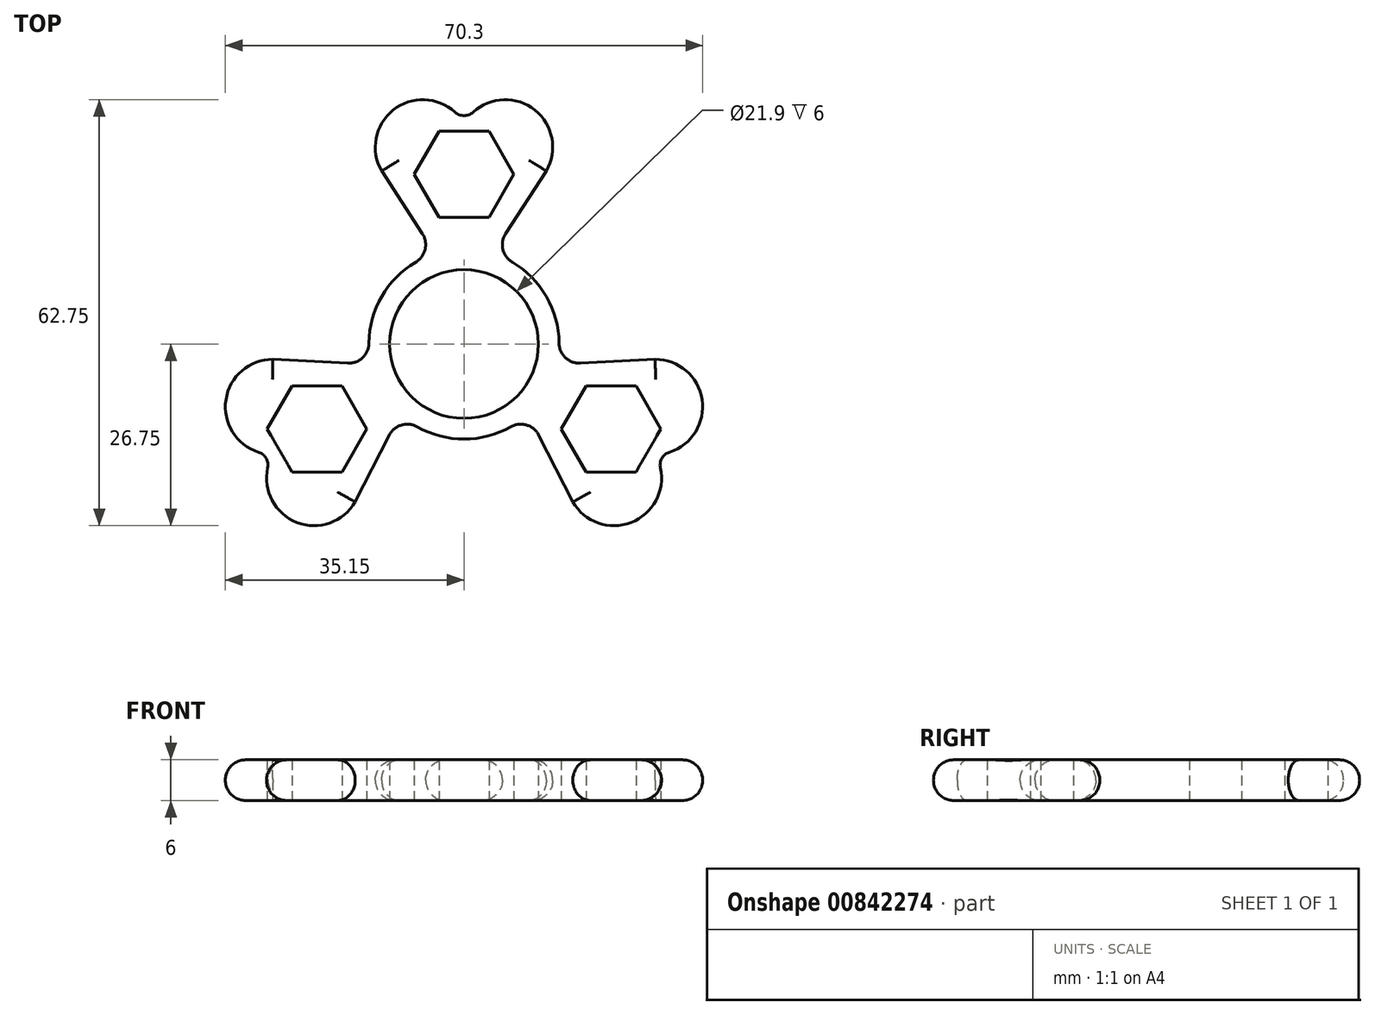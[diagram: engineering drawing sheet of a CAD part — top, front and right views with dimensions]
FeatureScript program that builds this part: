
annotation { "Feature Type Name" : "Feature", "Feature Type Description" : "" }
export const myFeature = defineFeature(function(context is Context, id is Id, definition is map)
    precondition{}
    {
        {
            var Q0;
            Q0=qCreatedBy(makeId("Top.planeOp"),FACE);
            var sketch = newSketch(context, id + "F0", { "sketchPlane" : qUnion([Q0])});
            skCircle(sketch, "E0", {"center": v(0, 0) * mm, "radius": 10.95 * mm});
            skCircle(sketch, "E1", {"center": v(0, 0) * mm, "radius": 14 * mm});
            skSolve(sketch);
        }
        {
            var Q0;
            Q0=makeQuery(id+"F0.imprint","IMPRINT",FACE,{"disambiguationData":[TD([[makeQuery(id+"F0.imprint","IMPRINT",EDGE,{"derivedFrom":sQuery(id+"F0.wireOp",EDGE,"E0")}),-1.0]])]});
            extrude(context, id + "F1", {"entities" : qUnion([Q0]), "depth" : 6 * mm, "offsetDistance" : 25 * mm});
        }
        {
            var Q0;
            Q0=qCreatedBy(makeId("Top.planeOp"),FACE);
            var sketch = newSketch(context, id + "F2", { "sketchPlane" : qUnion([Q0])});
            skLineSegment(sketch, "E2", {"start": v(6.13, 16.27) * mm, "end": v(12.12, 25.5) * mm});
            skArc(sketch, "E3", {"start": v(12.12, 25.5) * mm, "mid": v(10.45, 34.45) * mm, "end": v(1.35, 34.17) * mm});
            skLineSegment(sketch, "E4.trimOffspring", {"start": v(0, 32.5) * mm, "end": v(0, 67.1) * mm, "construction": true});
            skLineSegment(sketch, "E5.trimOffspring", {"start": v(0, 19) * mm, "end": v(0, 41) * mm, "construction": true});
            skArc(sketch, "E6.MirrorCS", {"start": v(-12.12, 25.5) * mm, "mid": v(-10.45, 34.45) * mm, "end": v(-1.35, 34.17) * mm});
            skPoint(sketch, "E7.visualSharp", {"position": v(0, 32.5) * mm});
            skArc(sketch, "E7.filletArc", {"start": v(-1.35, 34.17) * mm, "mid": v(0, 33.65) * mm, "end": v(1.35, 34.17) * mm});
            skCircle(sketch, "E8.cCircle", {"center": v(0, 25) * mm, "radius": 6.36 * mm, "construction": true});
            skLineSegment(sketch, "E8.0", {"start": v(-3.67, 31.36) * mm, "end": v(3.67, 31.36) * mm});
            skLineSegment(sketch, "E8.1", {"start": v(3.67, 31.36) * mm, "end": v(7.34, 25) * mm});
            skLineSegment(sketch, "E8.2", {"start": v(7.34, 25) * mm, "end": v(3.67, 18.64) * mm});
            skLineSegment(sketch, "E8.3", {"start": v(3.67, 18.64) * mm, "end": v(-3.67, 18.64) * mm});
            skLineSegment(sketch, "E8.4", {"start": v(-3.67, 18.64) * mm, "end": v(-7.34, 25) * mm});
            skLineSegment(sketch, "E8.5", {"start": v(-7.34, 25) * mm, "end": v(-3.67, 31.36) * mm});
            skPoint(sketch, "E8.0.midPoint", {"position": v(0, 31.36) * mm});
            skCircle(sketch, "E9.0", {"center": v(0, 0) * mm, "radius": 14 * mm});
            skArc(sketch, "E10", {"start": v(6.13, 16.27) * mm, "mid": v(5.73, 13.95) * mm, "end": v(7.12, 12.05) * mm});
            skPoint(sketch, "E11.orphan", {"position": v(1.19, 8.66) * mm});
            skPoint(sketch, "E12.orphan", {"position": v(-1.19, 8.66) * mm});
            skArc(sketch, "E13.MirrorCS", {"start": v(-6.13, 16.27) * mm, "mid": v(-5.73, 13.95) * mm, "end": v(-7.12, 12.05) * mm});
            skLineSegment(sketch, "E14", {"start": v(-6.13, 16.27) * mm, "end": v(-12.12, 25.5) * mm});
            skLineSegment(sketch, "E15.1.0", {"start": v(-25.32, -6.14) * mm, "end": v(-17.98, -6.14) * mm});
            skPoint(sketch, "E15.1.1", {"position": v(-28.15, -16.25) * mm});
            skPoint(sketch, "E15.1.2", {"position": v(-27.16, -15.68) * mm});
            skPoint(sketch, "E15.1.3", {"position": v(-8.1, -3.3) * mm});
            skArc(sketch, "E15.1.4", {"start": v(-28.15, -2.25) * mm, "mid": v(-35.06, -8.18) * mm, "end": v(-30.27, -15.92) * mm});
            skCircle(sketch, "E15.1.5", {"center": v(-21.65, -12.5) * mm, "radius": 6.36 * mm, "construction": true});
            skArc(sketch, "E15.1.6", {"start": v(-17.16, -2.83) * mm, "mid": v(-14.94, -2.02) * mm, "end": v(-14, 0.14) * mm});
            skLineSegment(sketch, "E15.1.7", {"start": v(-11.03, -13.44) * mm, "end": v(-16.02, -23.25) * mm});
            skLineSegment(sketch, "E15.1.8", {"start": v(-16.45, -9.5) * mm, "end": v(-35.5, -20.5) * mm, "construction": true});
            skLineSegment(sketch, "E15.1.9", {"start": v(-14.3, -12.5) * mm, "end": v(-17.98, -18.86) * mm});
            skLineSegment(sketch, "E15.1.10", {"start": v(-29, -12.5) * mm, "end": v(-25.32, -6.14) * mm});
            skArc(sketch, "E15.1.11", {"start": v(-16.02, -23.25) * mm, "mid": v(-24.61, -26.28) * mm, "end": v(-28.92, -18.25) * mm});
            skLineSegment(sketch, "E15.1.12", {"start": v(-17.16, -2.83) * mm, "end": v(-28.15, -2.25) * mm});
            skLineSegment(sketch, "E15.1.13", {"start": v(-17.98, -18.86) * mm, "end": v(-25.32, -18.86) * mm});
            skPoint(sketch, "E15.1.14", {"position": v(-6.9, -5.36) * mm});
            skLineSegment(sketch, "E15.1.15", {"start": v(-17.98, -6.14) * mm, "end": v(-14.3, -12.5) * mm});
            skArc(sketch, "E15.1.16", {"start": v(-11.03, -13.44) * mm, "mid": v(-9.22, -11.93) * mm, "end": v(-6.88, -12.2) * mm});
            skArc(sketch, "E15.1.17", {"start": v(-28.92, -18.25) * mm, "mid": v(-29.14, -16.83) * mm, "end": v(-30.27, -15.92) * mm});
            skLineSegment(sketch, "E15.1.18", {"start": v(-25.32, -18.86) * mm, "end": v(-29, -12.5) * mm});
            skLineSegment(sketch, "E15.2.0", {"start": v(17.98, -18.86) * mm, "end": v(14.3, -12.5) * mm});
            skPoint(sketch, "E15.2.1", {"position": v(28.15, -16.25) * mm});
            skPoint(sketch, "E15.2.2", {"position": v(27.16, -15.68) * mm});
            skPoint(sketch, "E15.2.3", {"position": v(6.9, -5.36) * mm});
            skArc(sketch, "E15.2.4", {"start": v(16.02, -23.25) * mm, "mid": v(24.61, -26.28) * mm, "end": v(28.92, -18.25) * mm});
            skCircle(sketch, "E15.2.5", {"center": v(21.65, -12.5) * mm, "radius": 6.36 * mm, "construction": true});
            skArc(sketch, "E15.2.6", {"start": v(11.03, -13.44) * mm, "mid": v(9.22, -11.93) * mm, "end": v(6.88, -12.2) * mm});
            skLineSegment(sketch, "E15.2.7", {"start": v(17.16, -2.83) * mm, "end": v(28.15, -2.25) * mm});
            skLineSegment(sketch, "E15.2.8", {"start": v(16.45, -9.5) * mm, "end": v(35.5, -20.5) * mm, "construction": true});
            skLineSegment(sketch, "E15.2.9", {"start": v(17.98, -6.14) * mm, "end": v(25.32, -6.14) * mm});
            skLineSegment(sketch, "E15.2.10", {"start": v(25.32, -18.86) * mm, "end": v(17.98, -18.86) * mm});
            skArc(sketch, "E15.2.11", {"start": v(28.15, -2.25) * mm, "mid": v(35.06, -8.18) * mm, "end": v(30.27, -15.92) * mm});
            skLineSegment(sketch, "E15.2.12", {"start": v(11.03, -13.44) * mm, "end": v(16.02, -23.25) * mm});
            skLineSegment(sketch, "E15.2.13", {"start": v(25.32, -6.14) * mm, "end": v(29, -12.5) * mm});
            skPoint(sketch, "E15.2.14", {"position": v(8.1, -3.3) * mm});
            skLineSegment(sketch, "E15.2.15", {"start": v(14.3, -12.5) * mm, "end": v(17.98, -6.14) * mm});
            skArc(sketch, "E15.2.16", {"start": v(17.16, -2.83) * mm, "mid": v(14.94, -2.02) * mm, "end": v(14, 0.14) * mm});
            skArc(sketch, "E15.2.17", {"start": v(30.27, -15.92) * mm, "mid": v(29.14, -16.83) * mm, "end": v(28.92, -18.25) * mm});
            skLineSegment(sketch, "E15.2.18", {"start": v(29, -12.5) * mm, "end": v(25.32, -18.86) * mm});
            skSolve(sketch);
        }
        {
            var Q0;
            Q0=makeQuery(id+"F2.imprint","IMPRINT",FACE,{"disambiguationData":[TD([[makeQuery(id+"F2.imprint","IMPRINT",EDGE,{"derivedFrom":sQuery(id+"F2.wireOp",EDGE,"E2")}),1.0]])]});
            var Q1;
            Q1=makeQuery(id+"F2.imprint","IMPRINT",FACE,{"disambiguationData":[TD([[makeQuery(id+"F2.imprint","IMPRINT",EDGE,{"derivedFrom":sQuery(id+"F2.wireOp",EDGE,"E15.1.0")}),1.0]])]});
            var Q2;
            Q2=makeQuery(id+"F2.imprint","IMPRINT",FACE,{"disambiguationData":[TD([[makeQuery(id+"F2.imprint","IMPRINT",EDGE,{"derivedFrom":sQuery(id+"F2.wireOp",EDGE,"E15.2.0")}),1.0]])]});
            extrude(context, id + "F3", {"entities" : qUnion([Q0, Q1, Q2]), "operationType" : NewBodyOperationType.ADD, "depth" : 6 * mm, "offsetDistance" : 25 * mm});
        }
        {
            var Q0;
            Q0=makeQuery(id+"F3.opExtrude","CAP_EDGE",EDGE,{"disambiguationData":[OSD([sQuery(id+"F2.wireOp",EDGE,"E14")])],"isStart":true});
            var Q1;
            Q1=makeQuery(id+"F3.opExtrude","CAP_EDGE",EDGE,{"disambiguationData":[OSD([sQuery(id+"F2.wireOp",EDGE,"E6.MirrorCS")])],"isStart":true});
            var Q2;
            Q2=makeQuery(id+"F3.opExtrude","CAP_EDGE",EDGE,{"disambiguationData":[OSD([sQuery(id+"F2.wireOp",EDGE,"E3")])],"isStart":true});
            var Q3;
            Q3=makeQuery(id+"F3.opExtrude","CAP_EDGE",EDGE,{"disambiguationData":[OSD([sQuery(id+"F2.wireOp",EDGE,"E7.filletArc")])],"isStart":true});
            var Q4;
            Q4=makeQuery(id+"F3.opExtrude","CAP_EDGE",EDGE,{"disambiguationData":[OSD([sQuery(id+"F2.wireOp",EDGE,"E2")])],"isStart":true});
            var Q5;
            Q5=makeQuery(id+"F3.opExtrude","CAP_EDGE",EDGE,{"disambiguationData":[OSD([sQuery(id+"F2.wireOp",EDGE,"E15.2.11")])],"isStart":true});
            var Q6;
            Q6=makeQuery(id+"F3.opExtrude","CAP_EDGE",EDGE,{"disambiguationData":[OSD([sQuery(id+"F2.wireOp",EDGE,"E15.2.17")])],"isStart":true});
            var Q7;
            Q7=makeQuery(id+"F3.opExtrude","CAP_EDGE",EDGE,{"disambiguationData":[OSD([sQuery(id+"F2.wireOp",EDGE,"E15.2.12")])],"isStart":true});
            var Q8;
            Q8=makeQuery(id+"F3.opExtrude","CAP_EDGE",EDGE,{"disambiguationData":[OSD([sQuery(id+"F2.wireOp",EDGE,"E15.1.11")])],"isStart":true});
            fillet(context, id + "F4", {"entities" : qUnion([Q0, Q1, Q2, Q3, Q4, Q5, Q6, Q7, Q8]), "radius" : 3 * mm, "tangentPropagation" : true, "allowEdgeOverflow" : false});
        }
        {
            var Q0;
            {var subQ2=sQuery(id+"F2.wireOp",EDGE,"E13.MirrorCS");var subQ3=sQuery(id+"F0.wireOp",EDGE,"E1");Q0=makeQuery(id+"F3.boolean.opBoolean","SPLIT",EDGE,{"disambiguationData":[TD([makeQuery(id+"F3.opExtrude","SWEPT_FACE",FACE,{"disambiguationData":[OSD([subQ2])]})])],"derivedFrom":makeQuery(id+"F1.opExtrude","CAP_EDGE",EDGE,{"disambiguationData":[OSD([subQ3])],"isStart":false})});}
            var Q1;
            Q1=makeQuery(id+"F3.opExtrude","CAP_EDGE",EDGE,{"disambiguationData":[OSD([sQuery(id+"F2.wireOp",EDGE,"E13.MirrorCS")])],"isStart":false});
            var Q2;
            Q2=makeQuery(id+"F3.opExtrude","CAP_EDGE",EDGE,{"disambiguationData":[OSD([sQuery(id+"F2.wireOp",EDGE,"E6.MirrorCS")])],"isStart":false});
            var Q3;
            Q3=makeQuery(id+"F3.opExtrude","CAP_EDGE",EDGE,{"disambiguationData":[OSD([sQuery(id+"F2.wireOp",EDGE,"E7.filletArc")])],"isStart":false});
            var Q4;
            Q4=makeQuery(id+"F3.opExtrude","CAP_EDGE",EDGE,{"disambiguationData":[OSD([sQuery(id+"F2.wireOp",EDGE,"E3")])],"isStart":false});
            var Q5;
            Q5=makeQuery(id+"F3.opExtrude","CAP_EDGE",EDGE,{"disambiguationData":[OSD([sQuery(id+"F2.wireOp",EDGE,"E2")])],"isStart":false});
            var Q6;
            Q6=makeQuery(id+"F3.opExtrude","CAP_EDGE",EDGE,{"disambiguationData":[OSD([sQuery(id+"F2.wireOp",EDGE,"E15.2.11")])],"isStart":false});
            var Q7;
            Q7=makeQuery(id+"F3.opExtrude","CAP_EDGE",EDGE,{"disambiguationData":[OSD([sQuery(id+"F2.wireOp",EDGE,"E15.2.17")])],"isStart":false});
            var Q8;
            Q8=makeQuery(id+"F3.opExtrude","CAP_EDGE",EDGE,{"disambiguationData":[OSD([sQuery(id+"F2.wireOp",EDGE,"E15.2.4")])],"isStart":false});
            var Q9;
            Q9=makeQuery(id+"F3.opExtrude","CAP_EDGE",EDGE,{"disambiguationData":[OSD([sQuery(id+"F2.wireOp",EDGE,"E15.2.12")])],"isStart":false});
            var Q10;
            Q10=makeQuery(id+"F3.opExtrude","CAP_EDGE",EDGE,{"disambiguationData":[OSD([sQuery(id+"F2.wireOp",EDGE,"E15.1.11")])],"isStart":false});
            var Q11;
            Q11=makeQuery(id+"F3.opExtrude","CAP_EDGE",EDGE,{"disambiguationData":[OSD([sQuery(id+"F2.wireOp",EDGE,"E15.1.17")])],"isStart":false});
            fillet(context, id + "F5", {"entities" : qUnion([Q0, Q1, Q2, Q3, Q4, Q5, Q6, Q7, Q8, Q9, Q10, Q11]), "radius" : 3 * mm, "tangentPropagation" : true, "allowEdgeOverflow" : false});
        }
    });
